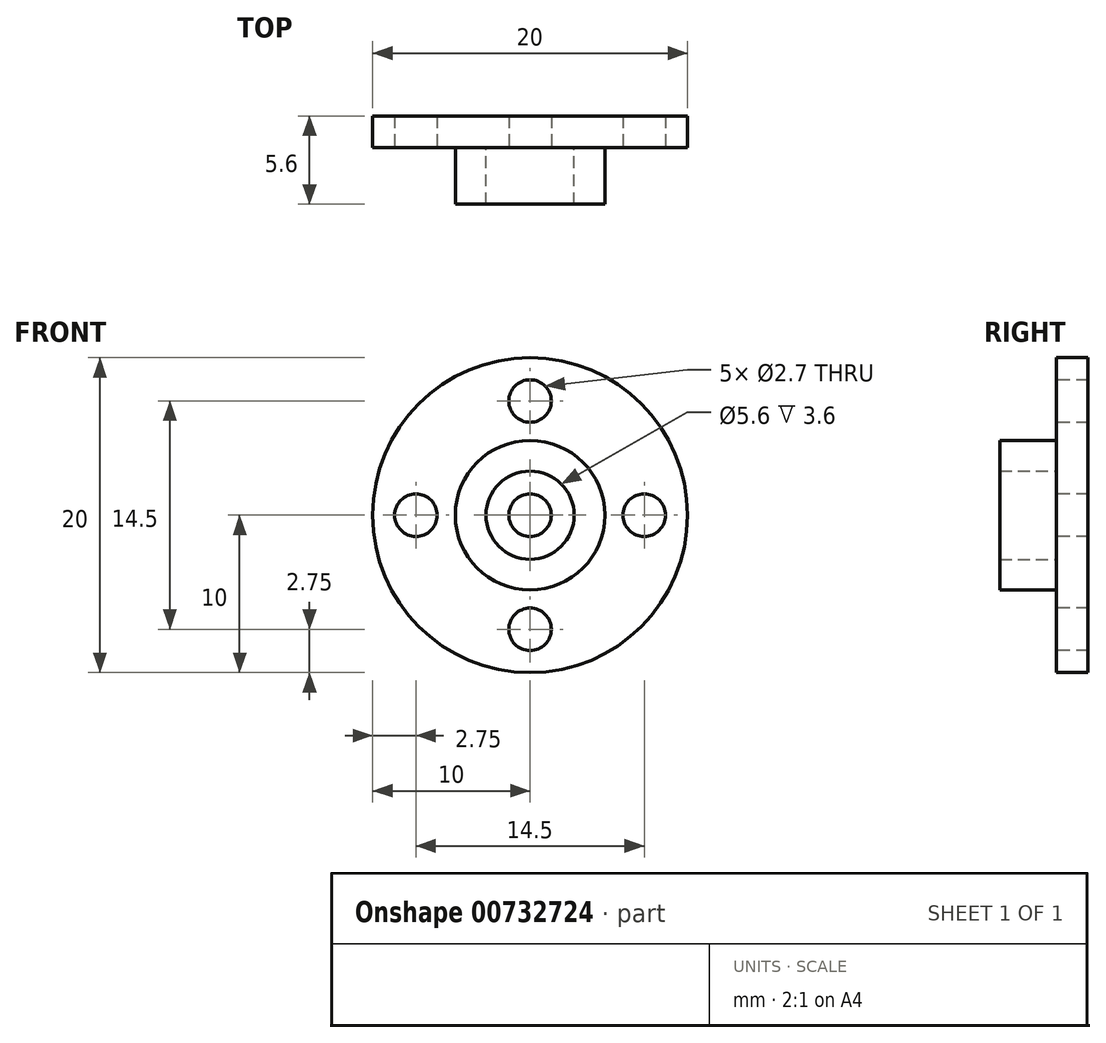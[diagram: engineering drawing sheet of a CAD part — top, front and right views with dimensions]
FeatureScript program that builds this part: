
annotation { "Feature Type Name" : "Feature", "Feature Type Description" : "" }
export const myFeature = defineFeature(function(context is Context, id is Id, definition is map)
    precondition{}
    {
        {
            var Q0;
            Q0=qCreatedBy(makeId("Front.planeOp"),FACE);
            var sketch = newSketch(context, id + "F0", { "sketchPlane" : qUnion([Q0])});
            skCircle(sketch, "E0", {"center": v(0, 0) * mm, "radius": 10 * mm});
            skSolve(sketch);
        }
        {
            var Q0;
            Q0=makeQuery(id+"F0.imprint","IMPRINT",FACE,{"disambiguationData":[TD([[makeQuery(id+"F0.imprint","IMPRINT",EDGE,{"derivedFrom":sQuery(id+"F0.wireOp",EDGE,"E0")}),1.0]])]});
            extrude(context, id + "F1", {"entities" : qUnion([Q0]), "depth" : 2 * mm});
        }
        {
            var Q0;
            Q0=makeQuery(id+"F1.opExtrude","CAP_FACE",FACE,{"disambiguationData":[OSD([sQuery(id+"F0.wireOp",EDGE,"E0")])],"isStart":false});
            var sketch = newSketch(context, id + "F2", { "sketchPlane" : qUnion([Q0])});
            skCircle(sketch, "E1", {"center": v(0, 0) * mm, "radius": 4.75 * mm});
            skCircle(sketch, "E2", {"center": v(0, 0) * mm, "radius": 2.8 * mm});
            skSolve(sketch);
        }
        {
            var Q0;
            Q0=makeQuery(id+"F2.imprint","IMPRINT",FACE,{"disambiguationData":[TD([[makeQuery(id+"F2.imprint","IMPRINT",EDGE,{"derivedFrom":sQuery(id+"F2.wireOp",EDGE,"E1")}),1.0]])]});
            extrude(context, id + "F3", {"entities" : qUnion([Q0]), "operationType" : NewBodyOperationType.ADD, "depth" : 3.6 * mm});
        }
        {
            var Q0;
            {var subQ0=sQuery(id+"F0.wireOp",EDGE,"E0");Q0=makeQuery(id+"F3.boolean.opBoolean","SPLIT",FACE,{"disambiguationData":[TD([makeQuery(id+"F1.opExtrude","SWEPT_FACE",FACE,{"disambiguationData":[OSD([subQ0])]})])],"derivedFrom":makeQuery(id+"F1.opExtrude","CAP_FACE",FACE,{"disambiguationData":[OSD([subQ0])],"isStart":false})});}
            var sketch = newSketch(context, id + "F4", { "sketchPlane" : qUnion([Q0])});
            skCircle(sketch, "E3", {"center": v(0, 7.25) * mm, "radius": 1.35 * mm});
            skCircle(sketch, "E4", {"center": v(7.25, 0) * mm, "radius": 1.35 * mm});
            skCircle(sketch, "E5", {"center": v(0, 0) * mm, "radius": 1.35 * mm});
            skCircle(sketch, "E6", {"center": v(0, -7.25) * mm, "radius": 1.35 * mm});
            skCircle(sketch, "E7", {"center": v(-7.25, 0) * mm, "radius": 1.35 * mm});
            skCircle(sketch, "E8", {"center": v(0, 0) * mm, "radius": 7.25 * mm, "construction": true});
            skSolve(sketch);
        }
        {
            var Q0;
            Q0=makeQuery(id+"F4.imprint","IMPRINT",FACE,{"disambiguationData":[TD([[makeQuery(id+"F4.imprint","IMPRINT",EDGE,{"derivedFrom":sQuery(id+"F4.wireOp",EDGE,"E3")}),1.0]])]});
            var Q1;
            Q1=makeQuery(id+"F4.imprint","IMPRINT",FACE,{"disambiguationData":[TD([[makeQuery(id+"F4.imprint","IMPRINT",EDGE,{"derivedFrom":sQuery(id+"F4.wireOp",EDGE,"E7")}),1.0]])]});
            var Q2;
            Q2=makeQuery(id+"F4.imprint","IMPRINT",FACE,{"disambiguationData":[TD([[makeQuery(id+"F4.imprint","IMPRINT",EDGE,{"derivedFrom":sQuery(id+"F4.wireOp",EDGE,"E5")}),1.0]])]});
            var Q3;
            Q3=makeQuery(id+"F4.imprint","IMPRINT",FACE,{"disambiguationData":[TD([[makeQuery(id+"F4.imprint","IMPRINT",EDGE,{"derivedFrom":sQuery(id+"F4.wireOp",EDGE,"E4")}),1.0]])]});
            var Q4;
            Q4=makeQuery(id+"F4.imprint","IMPRINT",FACE,{"disambiguationData":[TD([[makeQuery(id+"F4.imprint","IMPRINT",EDGE,{"derivedFrom":sQuery(id+"F4.wireOp",EDGE,"E6")}),1.0]])]});
            extrude(context, id + "F5", {"entities" : qUnion([Q0, Q1, Q2, Q3, Q4]), "operationType" : NewBodyOperationType.REMOVE, "oppositeDirection" : true, "depth" : 25 * mm});
        }
    });
